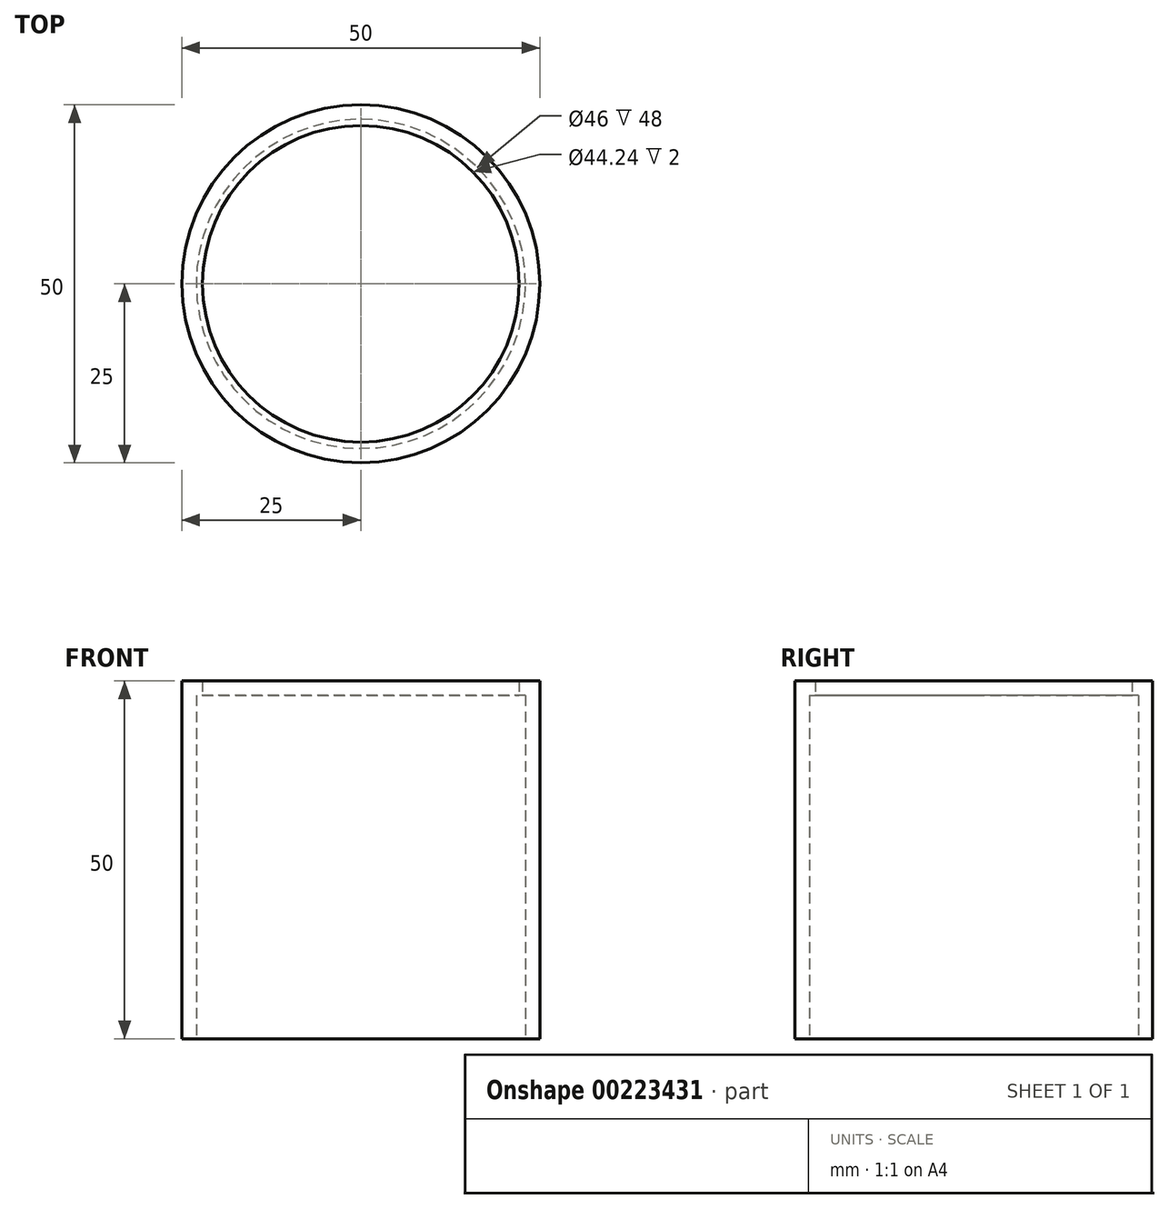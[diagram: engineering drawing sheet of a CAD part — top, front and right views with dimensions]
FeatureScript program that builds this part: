
annotation { "Feature Type Name" : "Feature", "Feature Type Description" : "" }
export const myFeature = defineFeature(function(context is Context, id is Id, definition is map)
    precondition{}
    {
        {
            var Q0;
            Q0=qCreatedBy(makeId("Top.planeOp"),FACE);
            var sketch = newSketch(context, id + "F0", { "sketchPlane" : qUnion([Q0])});
            skCircle(sketch, "E0", {"center": v(0, 0) * mm, "radius": 25 * mm});
            skSolve(sketch);
        }
        {
            var Q0;
            Q0 = qSketchRegion(id + "F0", true);
            var Q1;
            Q1=sQuery(id+"F0.wireOp",EDGE,"E0");
            extrude(context, id + "F1", {"entities" : qUnion([Q0]), "surfaceEntities" : qUnion([Q1]), "depth" : 50 * mm});
        }
        {
            var Q0;
            Q0=makeQuery(id+"F1.opExtrude","CAP_FACE",FACE,{"disambiguationData":[OSD([sQuery(id+"F0.wireOp",EDGE,"E0")])],"isStart":true});
            shell(context, id + "F2", {"entities" : qUnion([Q0]), "thickness" : 2 * mm});
        }
        {
            var Q0;
            {var subQ0=sQuery(id+"F0.wireOp",EDGE,"E0");Q0=makeQuery(id+"F2.opShell","OFFSET_FACE",FACE,{"disambiguationData":[OSD([subQ0]),TDD([makeQuery(id+"F1.opExtrude","CAP_FACE",FACE,{"disambiguationData":[OSD([subQ0])],"isStart":false})])]});}
            var sketch = newSketch(context, id + "F3", { "sketchPlane" : qUnion([Q0])});
            skCircle(sketch, "E1", {"center": v(0, 0) * mm, "radius": 22.12 * mm});
            skSolve(sketch);
        }
        {
            var Q0;
            Q0=makeQuery(id+"F3.imprint","IMPRINT",FACE,{"disambiguationData":[TD([[makeQuery(id+"F3.imprint","IMPRINT",EDGE,{"derivedFrom":sQuery(id+"F3.wireOp",EDGE,"E1")}),1.0]])]});
            extrude(context, id + "F4", {"entities" : qUnion([Q0]), "operationType" : NewBodyOperationType.REMOVE, "oppositeDirection" : true, "depth" : 25 * mm});
        }
    });
